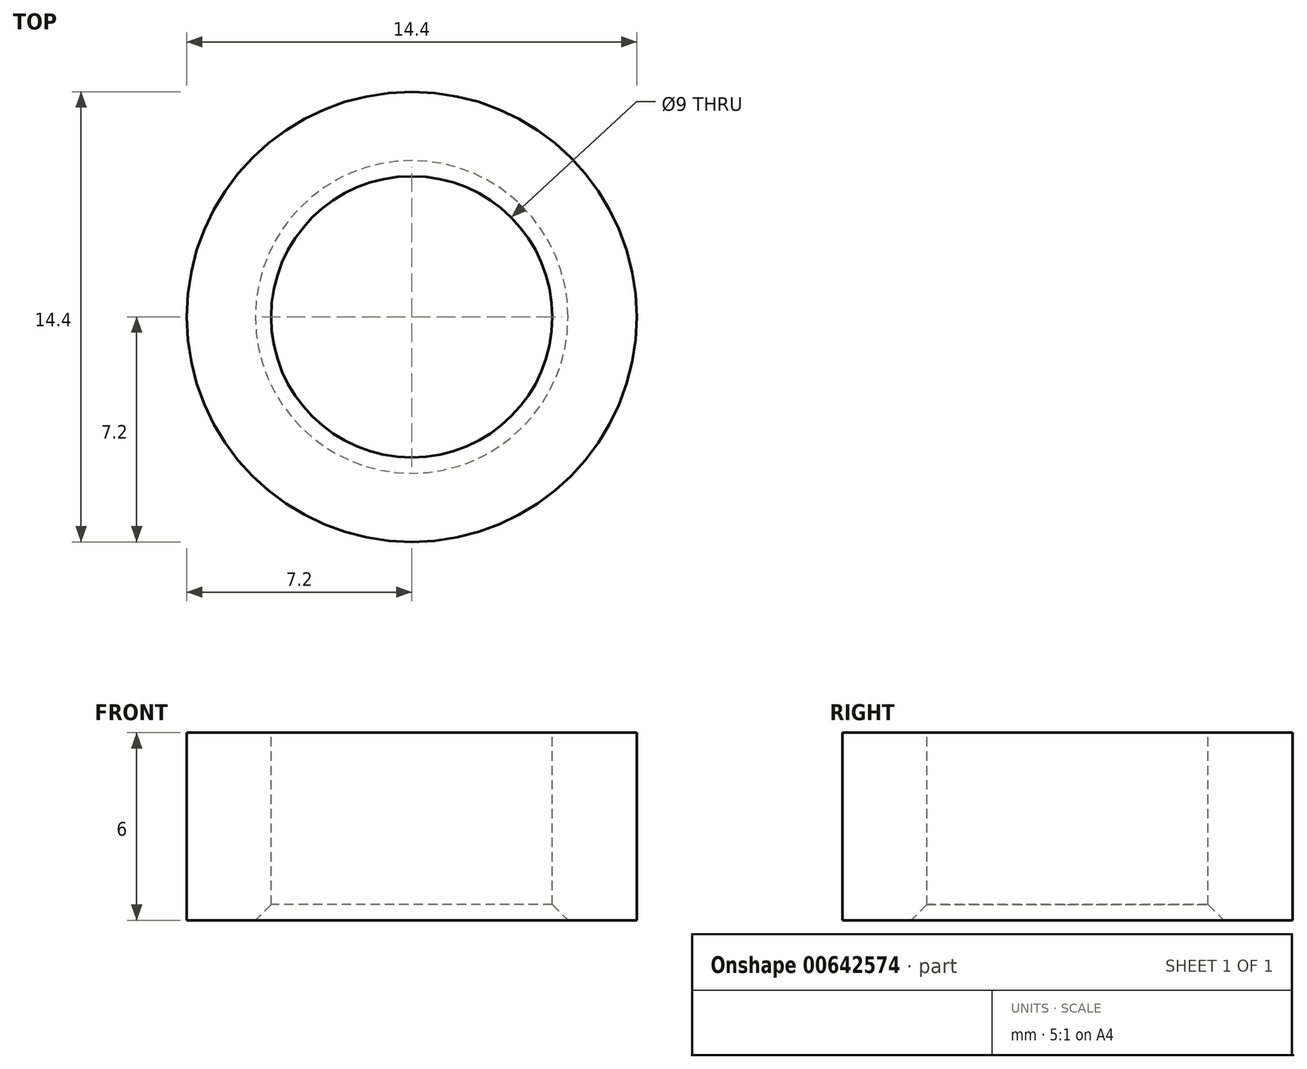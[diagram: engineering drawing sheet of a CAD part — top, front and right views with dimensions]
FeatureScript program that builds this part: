
annotation { "Feature Type Name" : "Feature", "Feature Type Description" : "" }
export const myFeature = defineFeature(function(context is Context, id is Id, definition is map)
    precondition{}
    {
        {
            var Q0;
            Q0=qCreatedBy(makeId("Top.planeOp"),FACE);
            var sketch = newSketch(context, id + "F0", { "sketchPlane" : qUnion([Q0])});
            skCircle(sketch, "E0", {"center": v(0, 0) * mm, "radius": 7.2 * mm});
            skSolve(sketch);
        }
        {
            var Q0;
            Q0 = qSketchRegion(id + "F0", true);
            extrude(context, id + "F1", {"entities" : qUnion([Q0]), "depth" : 6 * mm, "offsetDistance" : 25 * mm});
        }
        {
            var Q0;
            Q0=makeQuery(id+"F1.opExtrude","CAP_FACE",FACE,{"disambiguationData":[OSD([sQuery(id+"F0.wireOp",EDGE,"E0")])],"isStart":false});
            var sketch = newSketch(context, id + "F2", { "sketchPlane" : qUnion([Q0])});
            skCircle(sketch, "E1", {"center": v(0, 0) * mm, "radius": 4.5 * mm});
            skSolve(sketch);
        }
        {
            var Q0;
            Q0 = qSketchRegion(id + "F2", true);
            extrude(context, id + "F3", {"entities" : qUnion([Q0]), "operationType" : NewBodyOperationType.REMOVE, "endBound" : BoundingType.THROUGH_ALL, "oppositeDirection" : true, "depth" : 25 * mm, "offsetDistance" : 25 * mm});
        }
        {
            var Q0;
            Q0=makeQuery(id+"F3.boolean.opBoolean","COPY",EDGE,{"derivedFrom":makeQuery(id+"F3.opExtrude","CAP_EDGE",EDGE,{"disambiguationData":[OSD([sQuery(id+"F2.wireOp",EDGE,"E1")])],"isStart":true})});
            var Q1;
            Q1=makeQuery(id+"F3.boolean.opBoolean","INTERSECT",EDGE,{"derivedFrom":[makeQuery(id+"F1.opExtrude","CAP_FACE",FACE,{"disambiguationData":[OSD([sQuery(id+"F0.wireOp",EDGE,"E0")])],"isStart":true}),makeQuery(id+"F3.opExtrude","SWEPT_FACE",FACE,{"disambiguationData":[OSD([sQuery(id+"F2.wireOp",EDGE,"E1")])]})]});
            chamfer(context, id + "F4", {"entities" : qUnion([Q0, Q1]), "chamferType" : ChamferType.OFFSET_ANGLE, "width" : 0.5 * mm, "oppositeDirection" : false, "angle" : 45 * degree, "tangentPropagation" : true});
        }
    });
